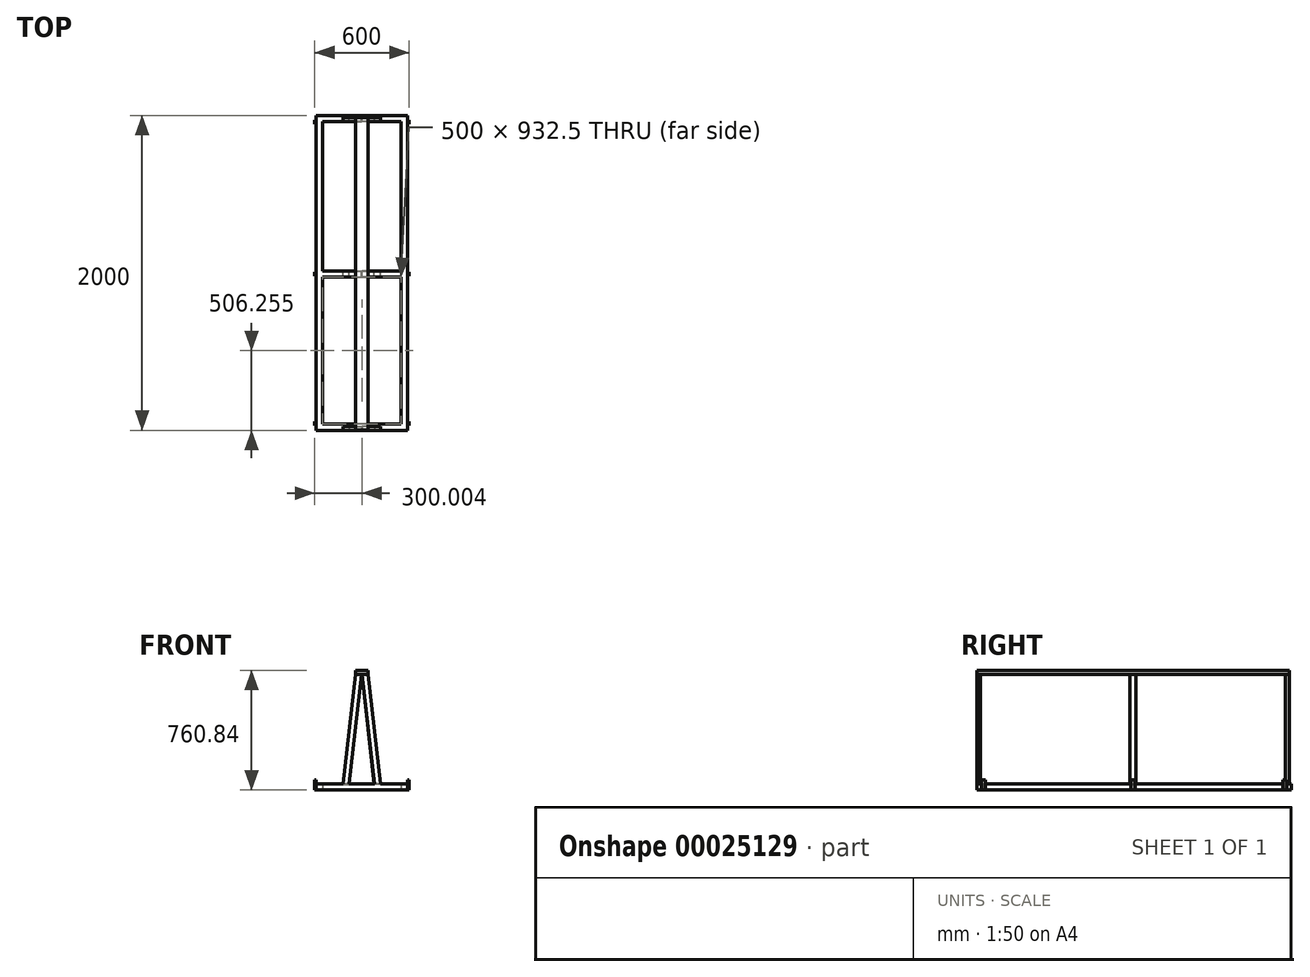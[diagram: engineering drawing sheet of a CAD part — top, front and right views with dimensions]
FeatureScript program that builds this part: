
annotation { "Feature Type Name" : "Feature", "Feature Type Description" : "" }
export const myFeature = defineFeature(function(context is Context, id is Id, definition is map)
    precondition{}
    {
        {
            var Q0;
            Q0=qCreatedBy(makeId("Top.planeOp"),FACE);
            var sketch = newSketch(context, id + "F0", { "sketchPlane" : qUnion([Q0])});
            skLineSegment(sketch, "E0.bottom", {"start": v(520.41, -87.36) * mm, "end": v(480.41, -87.36) * mm});
            skLineSegment(sketch, "E0.top", {"start": v(520.41, 1912.64) * mm, "end": v(480.41, 1912.64) * mm});
            skLineSegment(sketch, "E0.left", {"start": v(520.41, -87.36) * mm, "end": v(520.41, 1912.64) * mm});
            skLineSegment(sketch, "E0.right", {"start": v(480.41, -87.36) * mm, "end": v(480.41, 1912.64) * mm});
            skLineSegment(sketch, "E1.bottom", {"start": v(480.41, 1912.64) * mm, "end": v(-19.59, 1912.64) * mm});
            skLineSegment(sketch, "E1.top", {"start": v(480.41, 1872.64) * mm, "end": v(-19.59, 1872.64) * mm});
            skLineSegment(sketch, "E1.left", {"start": v(480.41, 1912.64) * mm, "end": v(480.41, 1872.64) * mm});
            skLineSegment(sketch, "E1.right", {"start": v(-19.59, 1912.64) * mm, "end": v(-19.59, 1872.64) * mm});
            skLineSegment(sketch, "E2.bottom", {"start": v(480.41, -87.36) * mm, "end": v(-19.59, -87.36) * mm});
            skLineSegment(sketch, "E2.top", {"start": v(480.41, -47.36) * mm, "end": v(-19.59, -47.36) * mm});
            skLineSegment(sketch, "E2.left", {"start": v(480.41, -87.36) * mm, "end": v(480.41, -47.36) * mm});
            skLineSegment(sketch, "E2.right", {"start": v(-19.59, -87.36) * mm, "end": v(-19.59, -47.36) * mm});
            skLineSegment(sketch, "E3.bottom", {"start": v(-19.59, -87.36) * mm, "end": v(-59.59, -87.36) * mm});
            skLineSegment(sketch, "E3.top", {"start": v(-19.59, 1912.64) * mm, "end": v(-59.59, 1912.64) * mm});
            skLineSegment(sketch, "E3.left", {"start": v(-19.59, -87.36) * mm, "end": v(-19.59, 1912.64) * mm});
            skLineSegment(sketch, "E3.right", {"start": v(-59.59, -87.36) * mm, "end": v(-59.59, 1912.64) * mm});
            skLineSegment(sketch, "E4.bottom", {"start": v(-19.59, 925.14) * mm, "end": v(480.41, 925.14) * mm});
            skLineSegment(sketch, "E4.top", {"start": v(-19.59, 885.14) * mm, "end": v(480.41, 885.14) * mm});
            skLineSegment(sketch, "E4.left", {"start": v(-19.59, 925.14) * mm, "end": v(-19.59, 885.14) * mm});
            skLineSegment(sketch, "E4.right", {"start": v(480.41, 925.14) * mm, "end": v(480.41, 885.14) * mm});
            skSolve(sketch);
        }
        {
            var Q0;
            {var subQ2=sQuery(id+"F0.wireOp",EDGE,"E2.bottom");Q0=makeQuery(id+"F0.imprint","IMPRINT",FACE,{"disambiguationData":[TD([[makeQuery(id+"F0.imprint","IMPRINT",EDGE,{"derivedFrom":subQ2}),-1.0]])]});}
            var Q1;
            Q1=makeQuery(id+"F0.imprint","IMPRINT",FACE,{"disambiguationData":[TD([[makeQuery(id+"F0.imprint","IMPRINT",EDGE,{"derivedFrom":sQuery(id+"F0.wireOp",EDGE,"E0.bottom")}),-1.0]])]});
            var Q2;
            {var subQ4=sQuery(id+"F0.wireOp",EDGE,"E3.bottom");Q2=makeQuery(id+"F0.imprint","IMPRINT",FACE,{"disambiguationData":[TD([[makeQuery(id+"F0.imprint","IMPRINT",EDGE,{"derivedFrom":subQ4}),-1.0]])]});}
            var Q3;
            {var subQ2=sQuery(id+"F0.wireOp",EDGE,"E1.bottom");Q3=makeQuery(id+"F0.imprint","IMPRINT",FACE,{"disambiguationData":[TD([[makeQuery(id+"F0.imprint","IMPRINT",EDGE,{"derivedFrom":subQ2}),1.0]])]});}
            var Q4;
            Q4=makeQuery(id+"F0.imprint","IMPRINT",FACE,{"disambiguationData":[TD([[makeQuery(id+"F0.imprint","IMPRINT",EDGE,{"derivedFrom":sQuery(id+"F0.wireOp",EDGE,"E4.bottom")}),-1.0]])]});
            extrude(context, id + "F1", {"entities" : qUnion([Q0, Q1, Q2, Q3, Q4]), "depth" : 40 * mm});
        }
        {
            var Q0;
            Q0=qCreatedBy(makeId("Top.planeOp"),FACE);
            var sketch = newSketch(context, id + "F2", { "sketchPlane" : qUnion([Q0])});
            skLineSegment(sketch, "E5.bottom", {"start": v(-59.59, -57.36) * mm, "end": v(-69.59, -57.36) * mm});
            skLineSegment(sketch, "E5.top", {"start": v(-59.59, -32.36) * mm, "end": v(-69.59, -32.36) * mm});
            skLineSegment(sketch, "E5.left", {"start": v(-59.59, -57.36) * mm, "end": v(-59.59, -32.36) * mm});
            skLineSegment(sketch, "E5.right", {"start": v(-69.59, -57.36) * mm, "end": v(-69.59, -32.36) * mm});
            skLineSegment(sketch, "E6.bottom", {"start": v(520.41, -57.36) * mm, "end": v(530.41, -57.36) * mm});
            skLineSegment(sketch, "E6.top", {"start": v(520.41, -32.36) * mm, "end": v(530.41, -32.36) * mm});
            skLineSegment(sketch, "E6.left", {"start": v(520.41, -57.36) * mm, "end": v(520.41, -32.36) * mm});
            skLineSegment(sketch, "E6.right", {"start": v(530.41, -57.36) * mm, "end": v(530.41, -32.36) * mm});
            skLineSegment(sketch, "E7.bottom", {"start": v(520.41, 1882.64) * mm, "end": v(530.41, 1882.64) * mm});
            skLineSegment(sketch, "E7.top", {"start": v(520.41, 1857.64) * mm, "end": v(530.41, 1857.64) * mm});
            skLineSegment(sketch, "E7.left", {"start": v(520.41, 1882.64) * mm, "end": v(520.41, 1857.64) * mm});
            skLineSegment(sketch, "E7.right", {"start": v(530.41, 1882.64) * mm, "end": v(530.41, 1857.64) * mm});
            skLineSegment(sketch, "E8.bottom", {"start": v(-69.59, 1882.64) * mm, "end": v(-59.59, 1882.64) * mm});
            skLineSegment(sketch, "E8.top", {"start": v(-69.59, 1857.64) * mm, "end": v(-59.59, 1857.64) * mm});
            skLineSegment(sketch, "E8.left", {"start": v(-69.59, 1882.64) * mm, "end": v(-69.59, 1857.64) * mm});
            skLineSegment(sketch, "E8.right", {"start": v(-59.59, 1882.64) * mm, "end": v(-59.59, 1857.64) * mm});
            skLineSegment(sketch, "E9.bottom", {"start": v(-69.59, 917.64) * mm, "end": v(-59.59, 917.64) * mm});
            skLineSegment(sketch, "E9.top", {"start": v(-69.59, 892.64) * mm, "end": v(-59.59, 892.64) * mm});
            skLineSegment(sketch, "E9.left", {"start": v(-69.59, 917.64) * mm, "end": v(-69.59, 892.64) * mm});
            skLineSegment(sketch, "E9.right", {"start": v(-59.59, 917.64) * mm, "end": v(-59.59, 892.64) * mm});
            skLineSegment(sketch, "E10.bottom", {"start": v(520.41, 917.64) * mm, "end": v(530.41, 917.64) * mm});
            skLineSegment(sketch, "E10.top", {"start": v(520.41, 892.64) * mm, "end": v(530.41, 892.64) * mm});
            skLineSegment(sketch, "E10.left", {"start": v(520.41, 917.64) * mm, "end": v(520.41, 892.64) * mm});
            skLineSegment(sketch, "E10.right", {"start": v(530.41, 917.64) * mm, "end": v(530.41, 892.64) * mm});
            skSolve(sketch);
        }
        {
            var Q0;
            Q0 = qSketchRegion(id + "F2", true);
            extrude(context, id + "F3", {"entities" : qUnion([Q0]), "operationType" : NewBodyOperationType.ADD, "depth" : 65 * mm});
        }
        {
            var Q0;
            Q0=makeQuery(id+"F1.opExtrude","SWEPT_FACE",FACE,{"disambiguationData":[OSD([sQuery(id+"F0.wireOp",EDGE,"E0.bottom"),sQuery(id+"F0.wireOp",EDGE,"E2.bottom"),sQuery(id+"F0.wireOp",EDGE,"E3.bottom")])]});
            var sketch = newSketch(context, id + "F4", { "sketchPlane" : qUnion([Q0])});
            skLineSegment(sketch, "E11.bottom", {"start": v(110.41, 39.56) * mm, "end": v(150.46, 40) * mm});
            skLineSegment(sketch, "E11.top", {"start": v(189.75, 735.84) * mm, "end": v(229.75, 735.84) * mm});
            skLineSegment(sketch, "E11.left", {"start": v(110.41, 39.56) * mm, "end": v(189.75, 735.84) * mm});
            skLineSegment(sketch, "E11.right", {"start": v(150.46, 40) * mm, "end": v(229.75, 735.84) * mm});
            skLineSegment(sketch, "E12", {"start": v(230.41, 0) * mm, "end": v(230.41, 194.8) * mm, "construction": true});
            skLineSegment(sketch, "E13.MirrorCS", {"start": v(310.36, 40) * mm, "end": v(231.08, 735.84) * mm});
            skLineSegment(sketch, "E14.MirrorCS", {"start": v(350.41, 39.56) * mm, "end": v(271.08, 735.84) * mm});
            skLineSegment(sketch, "E15.MirrorCS", {"start": v(271.08, 735.84) * mm, "end": v(231.08, 735.84) * mm});
            skLineSegment(sketch, "E16.MirrorCS", {"start": v(350.41, 39.56) * mm, "end": v(310.36, 40) * mm});
            skSolve(sketch);
        }
        {
            var Q0;
            {var subQ6=sQuery(id+"F4.wireOp",EDGE,"E11.top");Q0=makeQuery(id+"F4.imprint","IMPRINT",FACE,{"disambiguationData":[TD([[makeQuery(id+"F4.imprint","IMPRINT",EDGE,{"derivedFrom":subQ6}),-1.0]])]});}
            var Q1;
            {var subQ5=sQuery(id+"F4.wireOp",EDGE,"E13.MirrorCS");Q1=makeQuery(id+"F4.imprint","IMPRINT",FACE,{"disambiguationData":[TD([[makeQuery(id+"F4.imprint","IMPRINT",EDGE,{"derivedFrom":subQ5}),-1.0]])]});}
            extrude(context, id + "F5", {"entities" : qUnion([Q0, Q1]), "oppositeDirection" : true, "depth" : 25 * mm});
        }
        {
            var Q0;
            Q0=qCreatedBy(makeId("Front.planeOp"),FACE);
            cPlane(context, id + "F6", {"entities" : qUnion([Q0]), "cplaneType" : CPlaneType.OFFSET, "offset" : 905 * mm, "oppositeDirection" : true, "width" : 150 * mm, "height" : 150 * mm});
        }
        {
            var Q0;
            Q0=makeQuery(id+"F5.opExtrude","SWEPT_BODY",BODY,{"disambiguationData":[OSD([sQuery(id+"F0.wireOp",EDGE,"E0.bottom"),sQuery(id+"F0.wireOp",EDGE,"E2.bottom"),sQuery(id+"F0.wireOp",EDGE,"E3.bottom"),sQuery(id+"F4.wireOp",EDGE,"E13.MirrorCS"),sQuery(id+"F4.wireOp",EDGE,"E14.MirrorCS"),sQuery(id+"F4.wireOp",EDGE,"E15.MirrorCS"),sQuery(id+"F4.wireOp",EDGE,"E16.MirrorCS")])]});
            var Q1;
            Q1=makeQuery(id+"F5.opExtrude","SWEPT_BODY",BODY,{"disambiguationData":[OSD([sQuery(id+"F0.wireOp",EDGE,"E0.bottom"),sQuery(id+"F0.wireOp",EDGE,"E2.bottom"),sQuery(id+"F0.wireOp",EDGE,"E3.bottom"),sQuery(id+"F4.wireOp",EDGE,"E11.bottom"),sQuery(id+"F4.wireOp",EDGE,"E11.top"),sQuery(id+"F4.wireOp",EDGE,"E11.left"),sQuery(id+"F4.wireOp",EDGE,"E11.right")])]});
            var Q2;
            Q2=qCreatedBy(id+"F6.planeOp",FACE);
            mirror(context, id + "F7", {"operationType" : NewBodyOperationType.ADD, "entities" : qUnion([Q0, Q1]), "mirrorPlane" : qUnion([Q2])});
        }
        {
            var Q0;
            Q0=makeQuery(id+"F7.opPattern","COPY",FACE,{"derivedFrom":makeQuery(id+"F5.opExtrude","SWEPT_FACE",FACE,{"disambiguationData":[OSD([sQuery(id+"F4.wireOp",EDGE,"E11.top")])]}),"instanceName":"1"});
            var sketch = newSketch(context, id + "F8", { "sketchPlane" : qUnion([Q0])});
            skLineSegment(sketch, "E17.bottom", {"start": v(189.75, 1897.36) * mm, "end": v(270.93, 1897.36) * mm});
            skLineSegment(sketch, "E17.top", {"start": v(189.75, -85.5) * mm, "end": v(270.93, -85.5) * mm});
            skLineSegment(sketch, "E17.left", {"start": v(189.75, 1897.36) * mm, "end": v(189.75, -85.5) * mm});
            skLineSegment(sketch, "E17.right", {"start": v(270.93, 1897.36) * mm, "end": v(270.93, -85.5) * mm});
            skSolve(sketch);
        }
        {
            var Q0;
            Q0 = qSketchRegion(id + "F8", true);
            extrude(context, id + "F9", {"entities" : qUnion([Q0]), "operationType" : NewBodyOperationType.ADD, "depth" : 25 * mm});
        }
        {
            var Q0;
            Q0=qCreatedBy(id+"F6.planeOp",FACE);
            var sketch = newSketch(context, id + "F10", { "sketchPlane" : qUnion([Q0])});
            skLineSegment(sketch, "E18.bottom", {"start": v(90.9, 756.9) * mm, "end": v(90.9, 796.95) * mm});
            skLineSegment(sketch, "E18.top", {"start": v(90.9, 837.51) * mm, "end": v(90.9, 877.51) * mm});
            skLineSegment(sketch, "E18.left", {"start": v(90.9, 756.9) * mm, "end": v(90.9, 837.51) * mm});
            skLineSegment(sketch, "E18.right", {"start": v(90.9, 796.95) * mm, "end": v(90.9, 877.51) * mm});
            skLineSegment(sketch, "E19", {"start": v(90.9, 597) * mm, "end": v(90.9, 791.8) * mm, "construction": true});
            skLineSegment(sketch, "E20.MirrorCS", {"start": v(90.9, 877.51) * mm, "end": v(90.9, 796.95) * mm});
            skLineSegment(sketch, "E21.MirrorCS", {"start": v(90.9, 837.51) * mm, "end": v(90.9, 756.9) * mm});
            skLineSegment(sketch, "E22.MirrorCS", {"start": v(90.9, 877.51) * mm, "end": v(90.9, 837.51) * mm});
            skLineSegment(sketch, "E23.MirrorCS", {"start": v(90.9, 796.95) * mm, "end": v(90.9, 756.9) * mm});
            skLineSegment(sketch, "E24.bottom", {"start": v(109.51, 37.24) * mm, "end": v(149.56, 37.69) * mm});
            skLineSegment(sketch, "E24.top", {"start": v(188.84, 733.52) * mm, "end": v(228.84, 733.52) * mm});
            skLineSegment(sketch, "E24.left", {"start": v(109.51, 37.24) * mm, "end": v(188.84, 733.52) * mm});
            skLineSegment(sketch, "E24.right", {"start": v(149.56, 37.69) * mm, "end": v(228.84, 733.52) * mm});
            skLineSegment(sketch, "E25", {"start": v(229.51, -2.32) * mm, "end": v(229.51, 192.47) * mm, "construction": true});
            skLineSegment(sketch, "E26.MirrorCS", {"start": v(309.46, 37.69) * mm, "end": v(230.18, 733.52) * mm});
            skLineSegment(sketch, "E27.MirrorCS", {"start": v(349.51, 37.24) * mm, "end": v(270.18, 733.52) * mm});
            skLineSegment(sketch, "E28.MirrorCS", {"start": v(270.18, 733.52) * mm, "end": v(230.18, 733.52) * mm});
            skLineSegment(sketch, "E29.MirrorCS", {"start": v(349.51, 37.24) * mm, "end": v(309.46, 37.69) * mm});
            skSolve(sketch);
        }
        {
            var Q0;
            Q0=makeQuery(id+"F10.imprint","IMPRINT",FACE,{"disambiguationData":[TD([[makeQuery(id+"F10.imprint","IMPRINT",EDGE,{"derivedFrom":sQuery(id+"F10.wireOp",EDGE,"E24.bottom")}),1.0]])]});
            var Q1;
            Q1=makeQuery(id+"F10.imprint","IMPRINT",FACE,{"disambiguationData":[TD([[makeQuery(id+"F10.imprint","IMPRINT",EDGE,{"derivedFrom":sQuery(id+"F10.wireOp",EDGE,"E26.MirrorCS")}),-1.0]])]});
            var Q2;
            Q2=sQuery(id+"F10.wireOp",EDGE,"E24.bottom");
            var Q3;
            Q3=sQuery(id+"F10.wireOp",EDGE,"E24.top");
            var Q4;
            Q4=sQuery(id+"F10.wireOp",EDGE,"E24.left");
            var Q5;
            Q5=sQuery(id+"F10.wireOp",EDGE,"E24.right");
            var Q6;
            Q6=sQuery(id+"F10.wireOp",EDGE,"E26.MirrorCS");
            var Q7;
            Q7=sQuery(id+"F10.wireOp",EDGE,"E27.MirrorCS");
            var Q8;
            Q8=sQuery(id+"F10.wireOp",EDGE,"E28.MirrorCS");
            var Q9;
            Q9=sQuery(id+"F10.wireOp",EDGE,"E29.MirrorCS");
            var Q10;
            Q10=sQuery(id+"F0.wireOp",EDGE,"E4.top");
            extrude(context, id + "F11", {"entities" : qUnion([Q0, Q1]), "surfaceEntities" : qUnion([Q2, Q3, Q4, Q5, Q6, Q7, Q8, Q9, Q10]), "endBound" : BoundingType.SYMMETRIC, "depth" : 40 * mm});
        }
    });
